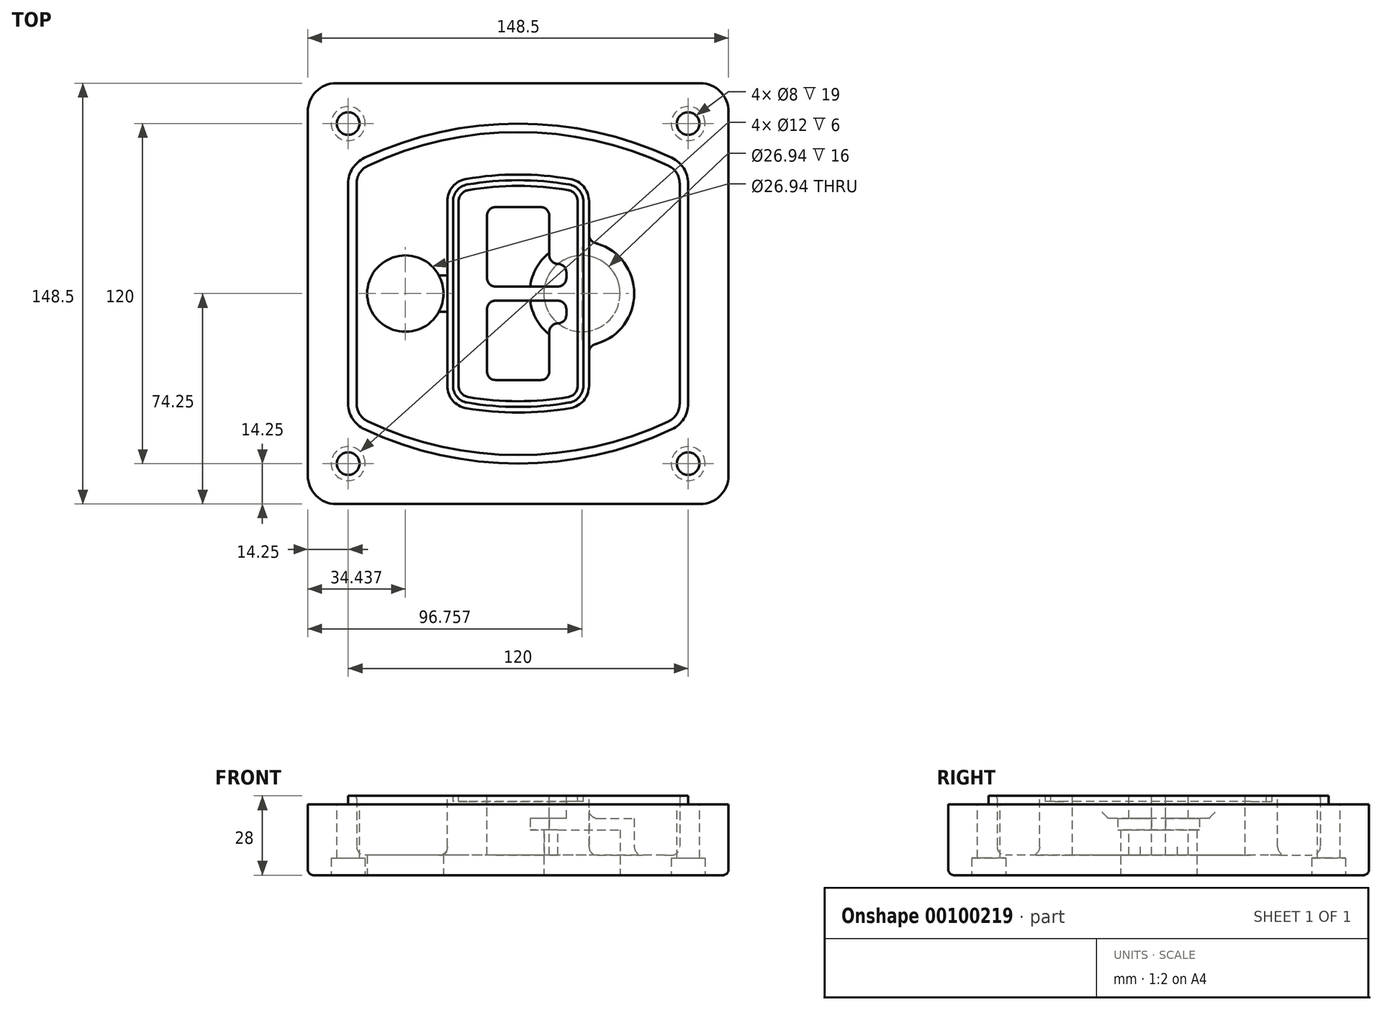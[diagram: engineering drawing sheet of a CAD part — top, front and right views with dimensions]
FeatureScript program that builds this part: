
annotation { "Feature Type Name" : "Feature", "Feature Type Description" : "" }
export const myFeature = defineFeature(function(context is Context, id is Id, definition is map)
    precondition{}
    {
        {
            var Q0;
            Q0=qCreatedBy(makeId("Top.planeOp"),FACE);
            var sketch = newSketch(context, id + "F0", { "sketchPlane" : qUnion([Q0])});
            skPoint(sketch, "E0.rect.middle", {"position": v(0, 0) * mm});
            skLineSegment(sketch, "E1.bottom", {"start": v(-64.25, -74.25) * mm, "end": v(64.25, -74.25) * mm});
            skLineSegment(sketch, "E1.top", {"start": v(-64.25, 74.25) * mm, "end": v(64.25, 74.25) * mm});
            skLineSegment(sketch, "E1.left", {"start": v(-74.25, -64.25) * mm, "end": v(-74.25, 64.25) * mm});
            skLineSegment(sketch, "E1.right", {"start": v(74.25, -64.25) * mm, "end": v(74.25, 64.25) * mm});
            skLineSegment(sketch, "E2", {"start": v(-74.25, 74.25) * mm, "end": v(74.25, -74.25) * mm, "construction": true});
            skLineSegment(sketch, "E3", {"start": v(74.25, 74.25) * mm, "end": v(-74.25, -74.25) * mm, "construction": true});
            skCircle(sketch, "E4", {"center": v(-60, 60) * mm, "radius": 4 * mm});
            skCircle(sketch, "E5", {"center": v(60, 60) * mm, "radius": 4 * mm});
            skCircle(sketch, "E6", {"center": v(60, -60) * mm, "radius": 4 * mm});
            skCircle(sketch, "E7", {"center": v(-60, -60) * mm, "radius": 4 * mm});
            skLineSegment(sketch, "E8", {"start": v(-60, 60) * mm, "end": v(60, 60) * mm, "construction": true});
            skLineSegment(sketch, "E9", {"start": v(60, 60) * mm, "end": v(60, -60) * mm, "construction": true});
            skLineSegment(sketch, "E10", {"start": v(60, -60) * mm, "end": v(-60, -60) * mm, "construction": true});
            skLineSegment(sketch, "E11", {"start": v(-60, -60) * mm, "end": v(-60, 60) * mm, "construction": true});
            skLineSegment(sketch, "E12", {"start": v(-60, 38.83) * mm, "end": v(-60, -38.83) * mm});
            skLineSegment(sketch, "E13", {"start": v(60, 38.83) * mm, "end": v(60, -38.83) * mm});
            skArc(sketch, "E14", {"start": v(54.26, 47.88) * mm, "mid": v(0, 60) * mm, "end": v(-54.26, 47.88) * mm});
            skArc(sketch, "E15", {"start": v(-54.26, -47.88) * mm, "mid": v(0, -60) * mm, "end": v(54.26, -47.88) * mm});
            skLineSegment(sketch, "E16", {"start": v(-60, 0) * mm, "end": v(60, 0) * mm, "construction": true});
            skPoint(sketch, "E17.visualSharp", {"position": v(-60, -45) * mm});
            skArc(sketch, "E17.filletArc", {"start": v(-60, -38.83) * mm, "mid": v(-58.44, -44.2) * mm, "end": v(-54.26, -47.88) * mm});
            skPoint(sketch, "E18.visualSharp", {"position": v(-60, 45) * mm});
            skArc(sketch, "E18.filletArc", {"start": v(-54.26, 47.88) * mm, "mid": v(-58.44, 44.2) * mm, "end": v(-60, 38.83) * mm});
            skPoint(sketch, "E19.visualSharp", {"position": v(60, 45) * mm});
            skArc(sketch, "E19.filletArc", {"start": v(60, 38.83) * mm, "mid": v(58.44, 44.2) * mm, "end": v(54.26, 47.88) * mm});
            skPoint(sketch, "E20.visualSharp", {"position": v(60, -45) * mm});
            skArc(sketch, "E20.filletArc", {"start": v(54.26, -47.88) * mm, "mid": v(58.44, -44.2) * mm, "end": v(60, -38.83) * mm});
            skPoint(sketch, "E21.visualSharp", {"position": v(-74.25, 74.25) * mm});
            skArc(sketch, "E21.filletArc", {"start": v(-64.25, 74.25) * mm, "mid": v(-71.32, 71.32) * mm, "end": v(-74.25, 64.25) * mm});
            skPoint(sketch, "E22.visualSharp", {"position": v(74.25, 74.25) * mm});
            skArc(sketch, "E22.filletArc", {"start": v(74.25, 64.25) * mm, "mid": v(71.32, 71.32) * mm, "end": v(64.25, 74.25) * mm});
            skPoint(sketch, "E23.visualSharp", {"position": v(74.25, -74.25) * mm});
            skArc(sketch, "E23.filletArc", {"start": v(64.25, -74.25) * mm, "mid": v(71.32, -71.32) * mm, "end": v(74.25, -64.25) * mm});
            skPoint(sketch, "E24.visualSharp", {"position": v(-74.25, -74.25) * mm});
            skArc(sketch, "E24.filletArc", {"start": v(-74.25, -64.25) * mm, "mid": v(-71.32, -71.32) * mm, "end": v(-64.25, -74.25) * mm});
            skArc(sketch, "E25.0", {"start": v(57, 38.83) * mm, "mid": v(55.9, 42.58) * mm, "end": v(52.98, 45.17) * mm});
            skLineSegment(sketch, "E25.1", {"start": v(57, 38.83) * mm, "end": v(57, -38.83) * mm});
            skArc(sketch, "E25.2", {"start": v(52.98, -45.17) * mm, "mid": v(55.9, -42.58) * mm, "end": v(57, -38.83) * mm});
            skArc(sketch, "E25.3", {"start": v(-52.98, -45.17) * mm, "mid": v(0, -57) * mm, "end": v(52.98, -45.17) * mm});
            skArc(sketch, "E25.4", {"start": v(-57, -38.83) * mm, "mid": v(-55.9, -42.58) * mm, "end": v(-52.98, -45.17) * mm});
            skArc(sketch, "E25.5", {"start": v(52.98, 45.17) * mm, "mid": v(0, 57) * mm, "end": v(-52.98, 45.17) * mm});
            skLineSegment(sketch, "E25.6", {"start": v(-57, 38.83) * mm, "end": v(-57, -38.83) * mm});
            skArc(sketch, "E25.7", {"start": v(-52.98, 45.17) * mm, "mid": v(-55.9, 42.58) * mm, "end": v(-57, 38.83) * mm});
            skArc(sketch, "E26.0", {"start": v(-55.96, 51.5) * mm, "mid": v(-61.82, 46.33) * mm, "end": v(-64, 38.83) * mm});
            skArc(sketch, "E26.1", {"start": v(55.96, 51.5) * mm, "mid": v(0, 64) * mm, "end": v(-55.96, 51.5) * mm});
            skArc(sketch, "E26.2", {"start": v(64, 38.83) * mm, "mid": v(61.82, 46.33) * mm, "end": v(55.96, 51.5) * mm});
            skLineSegment(sketch, "E26.3", {"start": v(64, 38.83) * mm, "end": v(64, -38.83) * mm});
            skArc(sketch, "E26.4", {"start": v(55.96, -51.5) * mm, "mid": v(61.82, -46.33) * mm, "end": v(64, -38.83) * mm});
            skLineSegment(sketch, "E26.5", {"start": v(-64, 38.83) * mm, "end": v(-64, -38.83) * mm});
            skArc(sketch, "E26.6", {"start": v(-55.96, -51.5) * mm, "mid": v(0, -64) * mm, "end": v(55.96, -51.5) * mm});
            skArc(sketch, "E26.7", {"start": v(-64, -38.83) * mm, "mid": v(-61.82, -46.33) * mm, "end": v(-55.96, -51.5) * mm});
            skSolve(sketch);
        }
        {
            var Q0;
            Q0=makeQuery(id+"F0.imprint","IMPRINT",FACE,{"disambiguationData":[TD([[makeQuery(id+"F0.imprint","IMPRINT",EDGE,{"derivedFrom":sQuery(id+"F0.wireOp",EDGE,"E1.bottom")}),1.0]])]});
            var Q1;
            Q1=makeQuery(id+"F0.imprint","IMPRINT",FACE,{"disambiguationData":[TD([[makeQuery(id+"F0.imprint","IMPRINT",EDGE,{"derivedFrom":sQuery(id+"F0.wireOp",EDGE,"E12")}),1.0]])]});
            var Q2;
            Q2=makeQuery(id+"F0.imprint","IMPRINT",FACE,{"disambiguationData":[TD([[makeQuery(id+"F0.imprint","IMPRINT",EDGE,{"derivedFrom":sQuery(id+"F0.wireOp",EDGE,"E25.0")}),1.0]])]});
            var Q3;
            Q3=makeQuery(id+"F0.imprint","IMPRINT",FACE,{"disambiguationData":[TD([[makeQuery(id+"F0.imprint","IMPRINT",EDGE,{"derivedFrom":sQuery(id+"F0.wireOp",EDGE,"E12")}),-1.0]])]});
            extrude(context, id + "F1", {"entities" : qUnion([Q0, Q1, Q2, Q3]), "oppositeDirection" : true, "depth" : 25 * mm});
        }
        {
            var Q0;
            Q0=makeQuery(id+"F0.imprint","IMPRINT",FACE,{"disambiguationData":[TD([[makeQuery(id+"F0.imprint","IMPRINT",EDGE,{"derivedFrom":sQuery(id+"F0.wireOp",EDGE,"E12")}),1.0]])]});
            extrude(context, id + "F2", {"entities" : qUnion([Q0]), "operationType" : NewBodyOperationType.ADD, "depth" : 3 * mm});
        }
        {
            var Q0;
            Q0=makeQuery(id+"F0.imprint","IMPRINT",FACE,{"disambiguationData":[TD([[makeQuery(id+"F0.imprint","IMPRINT",EDGE,{"derivedFrom":sQuery(id+"F0.wireOp",EDGE,"E25.0")}),1.0]])]});
            extrude(context, id + "F3", {"entities" : qUnion([Q0]), "operationType" : NewBodyOperationType.REMOVE, "oppositeDirection" : true, "depth" : 18 * mm});
        }
        {
            var Q0;
            Q0=makeQuery(id+"F2.opExtrude","CAP_FACE",FACE,{"disambiguationData":[OSD([sQuery(id+"F0.wireOp",EDGE,"E12"),sQuery(id+"F0.wireOp",EDGE,"E13"),sQuery(id+"F0.wireOp",EDGE,"E14"),sQuery(id+"F0.wireOp",EDGE,"E15"),sQuery(id+"F0.wireOp",EDGE,"E17.filletArc"),sQuery(id+"F0.wireOp",EDGE,"E18.filletArc"),sQuery(id+"F0.wireOp",EDGE,"E19.filletArc"),sQuery(id+"F0.wireOp",EDGE,"E20.filletArc"),sQuery(id+"F0.wireOp",EDGE,"E25.0"),sQuery(id+"F0.wireOp",EDGE,"E25.1"),sQuery(id+"F0.wireOp",EDGE,"E25.2"),sQuery(id+"F0.wireOp",EDGE,"E25.3"),sQuery(id+"F0.wireOp",EDGE,"E25.4"),sQuery(id+"F0.wireOp",EDGE,"E25.5"),sQuery(id+"F0.wireOp",EDGE,"E25.6"),sQuery(id+"F0.wireOp",EDGE,"E25.7")])],"isStart":false});
            var sketch = newSketch(context, id + "F4", { "sketchPlane" : qUnion([Q0])});
            skArc(sketch, "E27.0", {"start": v(-18.34, -40.45) * mm, "mid": v(0, -42) * mm, "end": v(18.34, -40.45) * mm});
            skArc(sketch, "E28.0", {"start": v(18.34, 40.45) * mm, "mid": v(0, 42) * mm, "end": v(-18.34, 40.45) * mm});
            skLineSegment(sketch, "E29", {"start": v(-25, 32.57) * mm, "end": v(-25, -32.57) * mm});
            skLineSegment(sketch, "E30", {"start": v(25, 32.57) * mm, "end": v(25, -32.57) * mm});
            skLineSegment(sketch, "E31", {"start": v(-25, 39.1) * mm, "end": v(25, 39.1) * mm, "construction": true});
            skLineSegment(sketch, "E32", {"start": v(-25, -39.1) * mm, "end": v(25, -39.1) * mm, "construction": true});
            skPoint(sketch, "E33.visualSharp", {"position": v(-25, 39.1) * mm});
            skArc(sketch, "E33.filletArc", {"start": v(-18.34, 40.45) * mm, "mid": v(-23.11, 37.73) * mm, "end": v(-25, 32.57) * mm});
            skPoint(sketch, "E34.visualSharp", {"position": v(25, 39.1) * mm});
            skArc(sketch, "E34.filletArc", {"start": v(25, 32.57) * mm, "mid": v(23.11, 37.73) * mm, "end": v(18.34, 40.45) * mm});
            skPoint(sketch, "E35.visualSharp", {"position": v(25, -39.1) * mm});
            skArc(sketch, "E35.filletArc", {"start": v(18.34, -40.45) * mm, "mid": v(23.11, -37.73) * mm, "end": v(25, -32.57) * mm});
            skPoint(sketch, "E36.visualSharp", {"position": v(-25, -39.1) * mm});
            skArc(sketch, "E36.filletArc", {"start": v(-25, -32.57) * mm, "mid": v(-23.11, -37.73) * mm, "end": v(-18.34, -40.45) * mm});
            skArc(sketch, "E37.0", {"start": v(52.98, 45.17) * mm, "mid": v(0, 57) * mm, "end": v(-52.98, 45.17) * mm});
            skArc(sketch, "E37.1", {"start": v(-52.98, 45.17) * mm, "mid": v(-55.9, 42.58) * mm, "end": v(-57, 38.83) * mm});
            skLineSegment(sketch, "E37.2", {"start": v(-57, 38.83) * mm, "end": v(-57, -38.83) * mm});
            skArc(sketch, "E37.3", {"start": v(-57, -38.83) * mm, "mid": v(-55.9, -42.58) * mm, "end": v(-52.98, -45.17) * mm});
            skArc(sketch, "E37.4", {"start": v(-52.98, -45.17) * mm, "mid": v(0, -57) * mm, "end": v(52.98, -45.17) * mm});
            skArc(sketch, "E37.5", {"start": v(52.98, -45.17) * mm, "mid": v(55.9, -42.58) * mm, "end": v(57, -38.83) * mm});
            skLineSegment(sketch, "E37.6", {"start": v(57, 38.83) * mm, "end": v(57, -38.83) * mm});
            skArc(sketch, "E37.7", {"start": v(57, 38.83) * mm, "mid": v(55.9, 42.58) * mm, "end": v(52.98, 45.17) * mm});
            skLineSegment(sketch, "E38.0", {"start": v(23, 32.57) * mm, "end": v(23, -32.57) * mm});
            skArc(sketch, "E38.1", {"start": v(18, -38.48) * mm, "mid": v(21.58, -36.44) * mm, "end": v(23, -32.57) * mm});
            skArc(sketch, "E38.2", {"start": v(-18, -38.48) * mm, "mid": v(0, -40) * mm, "end": v(18, -38.48) * mm});
            skArc(sketch, "E38.3", {"start": v(-23, -32.57) * mm, "mid": v(-21.58, -36.44) * mm, "end": v(-18, -38.48) * mm});
            skLineSegment(sketch, "E38.4", {"start": v(-23, 32.57) * mm, "end": v(-23, -32.57) * mm});
            skArc(sketch, "E38.5", {"start": v(23, 32.57) * mm, "mid": v(21.58, 36.44) * mm, "end": v(18, 38.48) * mm});
            skArc(sketch, "E38.6", {"start": v(-18, 38.48) * mm, "mid": v(-21.58, 36.44) * mm, "end": v(-23, 32.57) * mm});
            skArc(sketch, "E38.7", {"start": v(18, 38.48) * mm, "mid": v(0, 40) * mm, "end": v(-18, 38.48) * mm});
            skArc(sketch, "E39.0", {"start": v(21, 32.57) * mm, "mid": v(20.06, 35.15) * mm, "end": v(17.67, 36.5) * mm});
            skLineSegment(sketch, "E39.1", {"start": v(21, 32.57) * mm, "end": v(21, -32.57) * mm});
            skArc(sketch, "E39.2", {"start": v(17.67, -36.5) * mm, "mid": v(20.06, -35.15) * mm, "end": v(21, -32.57) * mm});
            skArc(sketch, "E39.3", {"start": v(-17.67, -36.5) * mm, "mid": v(0, -38) * mm, "end": v(17.67, -36.5) * mm});
            skArc(sketch, "E39.4", {"start": v(-21, -32.57) * mm, "mid": v(-20.06, -35.15) * mm, "end": v(-17.67, -36.5) * mm});
            skArc(sketch, "E39.5", {"start": v(17.67, 36.5) * mm, "mid": v(0, 38) * mm, "end": v(-17.67, 36.5) * mm});
            skLineSegment(sketch, "E39.6", {"start": v(-21, 32.57) * mm, "end": v(-21, -32.57) * mm});
            skArc(sketch, "E39.7", {"start": v(-17.67, 36.5) * mm, "mid": v(-20.06, 35.15) * mm, "end": v(-21, 32.57) * mm});
            skLineSegment(sketch, "E40", {"start": v(-25, 0) * mm, "end": v(25, 0) * mm, "construction": true});
            skLineSegment(sketch, "E41", {"start": v(-11, 5.5) * mm, "end": v(-11, 27.5) * mm});
            skLineSegment(sketch, "E42", {"start": v(-8, 30.5) * mm, "end": v(8, 30.5) * mm});
            skLineSegment(sketch, "E43", {"start": v(11, 27.5) * mm, "end": v(11, 13.5) * mm});
            skLineSegment(sketch, "E44", {"start": v(14, 10.5) * mm, "end": v(14, 10.5) * mm});
            skLineSegment(sketch, "E45", {"start": v(17, 7.5) * mm, "end": v(17, 5.5) * mm});
            skLineSegment(sketch, "E46", {"start": v(14, 2.5) * mm, "end": v(-8, 2.5) * mm});
            skPoint(sketch, "E47.visualSharp", {"position": v(-11, 30.5) * mm});
            skArc(sketch, "E47.filletArc", {"start": v(-8, 30.5) * mm, "mid": v(-10.12, 29.62) * mm, "end": v(-11, 27.5) * mm});
            skPoint(sketch, "E48.visualSharp", {"position": v(11, 30.5) * mm});
            skArc(sketch, "E48.filletArc", {"start": v(11, 27.5) * mm, "mid": v(10.12, 29.62) * mm, "end": v(8, 30.5) * mm});
            skPoint(sketch, "E49.visualSharp", {"position": v(11, 10.5) * mm});
            skArc(sketch, "E49.filletArc", {"start": v(11, 13.5) * mm, "mid": v(11.88, 11.38) * mm, "end": v(14, 10.5) * mm});
            skPoint(sketch, "E50.visualSharp", {"position": v(17, 10.5) * mm});
            skArc(sketch, "E50.filletArc", {"start": v(17, 7.5) * mm, "mid": v(16.12, 9.62) * mm, "end": v(14, 10.5) * mm});
            skPoint(sketch, "E51.visualSharp", {"position": v(17, 2.5) * mm});
            skArc(sketch, "E51.filletArc", {"start": v(14, 2.5) * mm, "mid": v(16.12, 3.38) * mm, "end": v(17, 5.5) * mm});
            skPoint(sketch, "E52.visualSharp", {"position": v(-11, 2.5) * mm});
            skArc(sketch, "E52.filletArc", {"start": v(-11, 5.5) * mm, "mid": v(-10.12, 3.38) * mm, "end": v(-8, 2.5) * mm});
            skLineSegment(sketch, "E53.0.MirrorCS", {"start": v(14, -2.5) * mm, "end": v(-8, -2.5) * mm});
            skArc(sketch, "E54.0.MirrorCS", {"start": v(-11, -5.5) * mm, "mid": v(-10.12, -3.38) * mm, "end": v(-8, -2.5) * mm});
            skLineSegment(sketch, "E55.0.MirrorCS", {"start": v(-11, -5.5) * mm, "end": v(-11, -27.5) * mm});
            skArc(sketch, "E56.0.MirrorCS", {"start": v(-8, -30.5) * mm, "mid": v(-10.12, -29.62) * mm, "end": v(-11, -27.5) * mm});
            skLineSegment(sketch, "E57.0.MirrorCS", {"start": v(-8, -30.5) * mm, "end": v(8, -30.5) * mm});
            skArc(sketch, "E58.0.MirrorCS", {"start": v(11, -27.5) * mm, "mid": v(10.12, -29.62) * mm, "end": v(8, -30.5) * mm});
            skLineSegment(sketch, "E59.0.MirrorCS", {"start": v(11, -27.5) * mm, "end": v(11, -13.5) * mm});
            skArc(sketch, "E60.0.MirrorCS", {"start": v(11, -13.5) * mm, "mid": v(11.88, -11.38) * mm, "end": v(14, -10.5) * mm});
            skArc(sketch, "E61.0.MirrorCS", {"start": v(17, -7.5) * mm, "mid": v(16.12, -9.62) * mm, "end": v(14, -10.5) * mm});
            skLineSegment(sketch, "E62.0.MirrorCS", {"start": v(17, -7.5) * mm, "end": v(17, -5.5) * mm});
            skArc(sketch, "E63.0.MirrorCS", {"start": v(14, -2.5) * mm, "mid": v(16.12, -3.38) * mm, "end": v(17, -5.5) * mm});
            skSolve(sketch);
        }
        {
            var Q0;
            Q0=makeQuery(id+"F4.imprint","IMPRINT",FACE,{"disambiguationData":[TD([[makeQuery(id+"F4.imprint","IMPRINT",EDGE,{"derivedFrom":sQuery(id+"F4.wireOp",EDGE,"E27.0")}),1.0]])]});
            var Q1;
            Q1=makeQuery(id+"F4.imprint","IMPRINT",FACE,{"disambiguationData":[TD([[makeQuery(id+"F4.imprint","IMPRINT",EDGE,{"derivedFrom":sQuery(id+"F4.wireOp",EDGE,"E38.0")}),-1.0]])]});
            var Q2;
            Q2=makeQuery(id+"F4.imprint","IMPRINT",FACE,{"disambiguationData":[TD([[makeQuery(id+"F4.imprint","IMPRINT",EDGE,{"derivedFrom":sQuery(id+"F4.wireOp",EDGE,"E39.0")}),1.0]])]});
            extrude(context, id + "F5", {"entities" : qUnion([Q0, Q1, Q2]), "operationType" : NewBodyOperationType.ADD, "endBound" : BoundingType.UP_TO_NEXT, "oppositeDirection" : true, "depth" : 25 * mm});
        }
        {
            var Q0;
            Q0=makeQuery(id+"F4.imprint","IMPRINT",FACE,{"disambiguationData":[TD([[makeQuery(id+"F4.imprint","IMPRINT",EDGE,{"derivedFrom":sQuery(id+"F4.wireOp",EDGE,"E38.0")}),-1.0]])]});
            extrude(context, id + "F6", {"entities" : qUnion([Q0]), "operationType" : NewBodyOperationType.REMOVE, "oppositeDirection" : true, "depth" : 2 * mm});
        }
        {
            var Q0;
            Q0=makeQuery(id+"F1.opExtrude","CAP_FACE",FACE,{"disambiguationData":[OSD([sQuery(id+"F0.wireOp",EDGE,"E1.bottom"),sQuery(id+"F0.wireOp",EDGE,"E1.top"),sQuery(id+"F0.wireOp",EDGE,"E1.left"),sQuery(id+"F0.wireOp",EDGE,"E1.right"),sQuery(id+"F0.wireOp",EDGE,"E4"),sQuery(id+"F0.wireOp",EDGE,"E5"),sQuery(id+"F0.wireOp",EDGE,"E6"),sQuery(id+"F0.wireOp",EDGE,"E7"),sQuery(id+"F0.wireOp",EDGE,"E21.filletArc"),sQuery(id+"F0.wireOp",EDGE,"E22.filletArc"),sQuery(id+"F0.wireOp",EDGE,"E23.filletArc"),sQuery(id+"F0.wireOp",EDGE,"E24.filletArc")])],"isStart":false});
            var sketch = newSketch(context, id + "F7", { "sketchPlane" : qUnion([Q0])});
            skCircle(sketch, "E64", {"center": v(22.5, 0) * mm, "radius": 13.47 * mm});
            skCircle(sketch, "E65", {"center": v(-39.81, 0) * mm, "radius": 13.47 * mm});
            skLineSegment(sketch, "E66", {"start": v(74.25, 0) * mm, "end": v(-74.25, 0) * mm});
            skCircle(sketch, "E67", {"center": v(22.5, 0) * mm, "radius": 18.47 * mm});
            skCircle(sketch, "E68", {"center": v(60, -60) * mm, "radius": 6 * mm});
            skCircle(sketch, "E69", {"center": v(-60, -60) * mm, "radius": 6 * mm});
            skCircle(sketch, "E70", {"center": v(-60, 60) * mm, "radius": 6 * mm});
            skCircle(sketch, "E71", {"center": v(60, 60) * mm, "radius": 6 * mm});
            skSolve(sketch);
        }
        {
            var Q0;
            {var subQ1=sQuery(id+"F7.wireOp",EDGE,"E66");var subQ4=sQuery(id+"F7.wireOp",EDGE,"E64");var subQ6=makeQuery(id+"F7.imprint","INTERSECT",VERTEX,{"disambiguationData":[OD(0.0)],"derivedFrom":[subQ4,subQ1]});Q0=makeQuery(id+"F7.imprint","IMPRINT",FACE,{"disambiguationData":[TD([[makeQuery(id+"F7.imprint","IMPRINT",EDGE,{"disambiguationData":[TD([[subQ6,-1.0]])],"derivedFrom":subQ4}),-1.0]])]});}
            var Q1;
            {var subQ0=sQuery(id+"F7.wireOp",EDGE,"E66");var subQ1=sQuery(id+"F7.wireOp",EDGE,"E64");var subQ3=makeQuery(id+"F7.imprint","INTERSECT",VERTEX,{"disambiguationData":[OD(0.0)],"derivedFrom":[subQ1,subQ0]});Q1=makeQuery(id+"F7.imprint","IMPRINT",FACE,{"disambiguationData":[TD([[makeQuery(id+"F7.imprint","IMPRINT",EDGE,{"disambiguationData":[TD([[subQ3,-1.0]])],"derivedFrom":subQ1}),1.0]])]});}
            var Q2;
            {var subQ0=sQuery(id+"F7.wireOp",EDGE,"E66");var subQ1=sQuery(id+"F7.wireOp",EDGE,"E64");var subQ3=makeQuery(id+"F7.imprint","INTERSECT",VERTEX,{"disambiguationData":[OD(0.0)],"derivedFrom":[subQ1,subQ0]});Q2=makeQuery(id+"F7.imprint","IMPRINT",FACE,{"disambiguationData":[TD([[makeQuery(id+"F7.imprint","IMPRINT",EDGE,{"disambiguationData":[TD([[subQ3,1.0]])],"derivedFrom":subQ1}),1.0]])]});}
            var Q3;
            {var subQ1=sQuery(id+"F7.wireOp",EDGE,"E66");var subQ4=sQuery(id+"F7.wireOp",EDGE,"E64");var subQ6=makeQuery(id+"F7.imprint","INTERSECT",VERTEX,{"disambiguationData":[OD(0.0)],"derivedFrom":[subQ4,subQ1]});Q3=makeQuery(id+"F7.imprint","IMPRINT",FACE,{"disambiguationData":[TD([[makeQuery(id+"F7.imprint","IMPRINT",EDGE,{"disambiguationData":[TD([[subQ6,1.0]])],"derivedFrom":subQ4}),-1.0]])]});}
            extrude(context, id + "F8", {"entities" : qUnion([Q0, Q1, Q2, Q3]), "operationType" : NewBodyOperationType.ADD, "oppositeDirection" : true, "depth" : 20 * mm});
        }
        {
            var Q0;
            {var subQ0=sQuery(id+"F7.wireOp",EDGE,"E66");var subQ1=sQuery(id+"F7.wireOp",EDGE,"E64");var subQ3=makeQuery(id+"F7.imprint","INTERSECT",VERTEX,{"disambiguationData":[OD(0.0)],"derivedFrom":[subQ1,subQ0]});Q0=makeQuery(id+"F7.imprint","IMPRINT",FACE,{"disambiguationData":[TD([[makeQuery(id+"F7.imprint","IMPRINT",EDGE,{"disambiguationData":[TD([[subQ3,-1.0]])],"derivedFrom":subQ1}),1.0]])]});}
            var Q1;
            {var subQ0=sQuery(id+"F7.wireOp",EDGE,"E66");var subQ1=sQuery(id+"F7.wireOp",EDGE,"E64");var subQ3=makeQuery(id+"F7.imprint","INTERSECT",VERTEX,{"disambiguationData":[OD(0.0)],"derivedFrom":[subQ1,subQ0]});Q1=makeQuery(id+"F7.imprint","IMPRINT",FACE,{"disambiguationData":[TD([[makeQuery(id+"F7.imprint","IMPRINT",EDGE,{"disambiguationData":[TD([[subQ3,1.0]])],"derivedFrom":subQ1}),1.0]])]});}
            extrude(context, id + "F9", {"entities" : qUnion([Q0, Q1]), "operationType" : NewBodyOperationType.REMOVE, "oppositeDirection" : true, "depth" : 16 * mm});
        }
        {
            var Q0;
            {var subQ0=sQuery(id+"F7.wireOp",EDGE,"E66");var subQ1=sQuery(id+"F7.wireOp",EDGE,"E65");var subQ3=makeQuery(id+"F7.imprint","INTERSECT",VERTEX,{"disambiguationData":[OD(0.0)],"derivedFrom":[subQ1,subQ0]});Q0=makeQuery(id+"F7.imprint","IMPRINT",FACE,{"disambiguationData":[TD([[makeQuery(id+"F7.imprint","IMPRINT",EDGE,{"disambiguationData":[TD([[subQ3,-1.0]])],"derivedFrom":subQ1}),1.0]])]});}
            var Q1;
            {var subQ0=sQuery(id+"F7.wireOp",EDGE,"E66");var subQ1=sQuery(id+"F7.wireOp",EDGE,"E65");var subQ3=makeQuery(id+"F7.imprint","INTERSECT",VERTEX,{"disambiguationData":[OD(0.0)],"derivedFrom":[subQ1,subQ0]});Q1=makeQuery(id+"F7.imprint","IMPRINT",FACE,{"disambiguationData":[TD([[makeQuery(id+"F7.imprint","IMPRINT",EDGE,{"disambiguationData":[TD([[subQ3,1.0]])],"derivedFrom":subQ1}),1.0]])]});}
            extrude(context, id + "F10", {"entities" : qUnion([Q0, Q1]), "operationType" : NewBodyOperationType.REMOVE, "oppositeDirection" : true, "depth" : 25 * mm});
        }
        {
            var Q0;
            Q0=makeQuery(id+"F7.imprint","IMPRINT",FACE,{"disambiguationData":[TD([[makeQuery(id+"F7.imprint","IMPRINT",EDGE,{"derivedFrom":sQuery(id+"F7.wireOp",EDGE,"E68")}),1.0]])]});
            var Q1;
            Q1=makeQuery(id+"F7.imprint","IMPRINT",FACE,{"disambiguationData":[TD([[makeQuery(id+"F7.imprint","IMPRINT",EDGE,{"derivedFrom":makeQuery(id+"F1.opExtrude","CAP_EDGE",EDGE,{"disambiguationData":[OSD([sQuery(id+"F0.wireOp",EDGE,"E5")])],"isStart":false})}),-1.0]])]});
            var Q2;
            Q2=makeQuery(id+"F7.imprint","IMPRINT",FACE,{"disambiguationData":[TD([[makeQuery(id+"F7.imprint","IMPRINT",EDGE,{"derivedFrom":sQuery(id+"F7.wireOp",EDGE,"E69")}),1.0]])]});
            var Q3;
            Q3=makeQuery(id+"F7.imprint","IMPRINT",FACE,{"disambiguationData":[TD([[makeQuery(id+"F7.imprint","IMPRINT",EDGE,{"derivedFrom":makeQuery(id+"F1.opExtrude","CAP_EDGE",EDGE,{"disambiguationData":[OSD([sQuery(id+"F0.wireOp",EDGE,"E4")])],"isStart":false})}),-1.0]])]});
            var Q4;
            Q4=makeQuery(id+"F7.imprint","IMPRINT",FACE,{"disambiguationData":[TD([[makeQuery(id+"F7.imprint","IMPRINT",EDGE,{"derivedFrom":sQuery(id+"F7.wireOp",EDGE,"E70")}),1.0]])]});
            var Q5;
            Q5=makeQuery(id+"F7.imprint","IMPRINT",FACE,{"disambiguationData":[TD([[makeQuery(id+"F7.imprint","IMPRINT",EDGE,{"derivedFrom":makeQuery(id+"F1.opExtrude","CAP_EDGE",EDGE,{"disambiguationData":[OSD([sQuery(id+"F0.wireOp",EDGE,"E7")])],"isStart":false})}),-1.0]])]});
            var Q6;
            Q6=makeQuery(id+"F7.imprint","IMPRINT",FACE,{"disambiguationData":[TD([[makeQuery(id+"F7.imprint","IMPRINT",EDGE,{"derivedFrom":sQuery(id+"F7.wireOp",EDGE,"E71")}),1.0]])]});
            var Q7;
            Q7=makeQuery(id+"F7.imprint","IMPRINT",FACE,{"disambiguationData":[TD([[makeQuery(id+"F7.imprint","IMPRINT",EDGE,{"derivedFrom":makeQuery(id+"F1.opExtrude","CAP_EDGE",EDGE,{"disambiguationData":[OSD([sQuery(id+"F0.wireOp",EDGE,"E6")])],"isStart":false})}),-1.0]])]});
            extrude(context, id + "F11", {"entities" : qUnion([Q0, Q1, Q2, Q3, Q4, Q5, Q6, Q7]), "operationType" : NewBodyOperationType.REMOVE, "oppositeDirection" : true, "depth" : 6 * mm});
        }
        {
            var Q0;
            Q0=makeQuery(id+"F9.boolean.opBoolean","COPY",FACE,{"derivedFrom":makeQuery(id+"F9.opExtrude","CAP_FACE",FACE,{"disambiguationData":[OSD([sQuery(id+"F7.wireOp",EDGE,"E64")])],"isStart":false})});
            var sketch = newSketch(context, id + "F12", { "sketchPlane" : qUnion([Q0])});
            skArc(sketch, "E72.0", {"start": v(11, 14.45) * mm, "mid": v(6.45, 9.13) * mm, "end": v(4.2, 2.5) * mm});
            skArc(sketch, "E72.1", {"start": v(4.2, -2.5) * mm, "mid": v(6.45, -9.13) * mm, "end": v(11, -14.45) * mm});
            skLineSegment(sketch, "E73", {"start": v(4.2, -2.5) * mm, "end": v(14, -2.5) * mm});
            skLineSegment(sketch, "E74.0", {"start": v(14, 2.5) * mm, "end": v(4.2, 2.5) * mm});
            skArc(sketch, "E74.1", {"start": v(14, 2.5) * mm, "mid": v(16.12, 3.38) * mm, "end": v(17, 5.5) * mm});
            skLineSegment(sketch, "E74.2", {"start": v(17, 7.5) * mm, "end": v(17, 5.5) * mm});
            skArc(sketch, "E74.3", {"start": v(17, 7.5) * mm, "mid": v(16.12, 9.62) * mm, "end": v(14, 10.5) * mm});
            skArc(sketch, "E74.4", {"start": v(11, 13.5) * mm, "mid": v(11.88, 11.38) * mm, "end": v(14, 10.5) * mm});
            skLineSegment(sketch, "E74.5", {"start": v(11, 14.45) * mm, "end": v(11, 13.5) * mm});
            skLineSegment(sketch, "E74.7", {"start": v(14, -2.5) * mm, "end": v(4.2, -2.5) * mm});
            skArc(sketch, "E74.8", {"start": v(14, -2.5) * mm, "mid": v(16.12, -3.38) * mm, "end": v(17, -5.5) * mm});
            skLineSegment(sketch, "E74.9", {"start": v(17, -7.5) * mm, "end": v(17, -5.5) * mm});
            skArc(sketch, "E74.10", {"start": v(17, -7.5) * mm, "mid": v(16.12, -9.62) * mm, "end": v(14, -10.5) * mm});
            skArc(sketch, "E74.11", {"start": v(11, -13.5) * mm, "mid": v(11.88, -11.38) * mm, "end": v(14, -10.5) * mm});
            skLineSegment(sketch, "E74.12", {"start": v(11, -14.45) * mm, "end": v(11, -13.5) * mm});
            skPoint(sketch, "E75.orphan", {"position": v(11, -27.5) * mm});
            skPoint(sketch, "E76.orphan", {"position": v(-8, -2.5) * mm});
            skPoint(sketch, "E77.orphan", {"position": v(-8, 2.5) * mm});
            skPoint(sketch, "E78.orphan", {"position": v(11, 27.5) * mm});
            skSolve(sketch);
        }
        {
            var Q0;
            {var subQ7=sQuery(id+"F12.wireOp",EDGE,"E72.0");var subQ14=sQuery(id+"F12.wireOp",EDGE,"E72.1");var subQ16=sQuery(id+"F12.wireOp",EDGE,"E74.1");var subQ18=sQuery(id+"F12.wireOp",EDGE,"E74.8");Q0=qUnion([makeQuery(id+"F12.imprint","IMPRINT",FACE,{"disambiguationData":[TD([[makeQuery(id+"F12.imprint","IMPRINT",EDGE,{"derivedFrom":subQ7}),1.0]])]}),makeQuery(id+"F12.imprint","IMPRINT",FACE,{"disambiguationData":[TD([[makeQuery(id+"F12.imprint","IMPRINT",EDGE,{"derivedFrom":subQ14}),1.0]])]}),makeQuery(id+"F12.imprint","IMPRINT",FACE,{"disambiguationData":[TD([[makeQuery(id+"F12.imprint","IMPRINT",EDGE,{"derivedFrom":subQ16}),1.0]])]}),makeQuery(id+"F12.imprint","IMPRINT",FACE,{"disambiguationData":[TD([[makeQuery(id+"F12.imprint","IMPRINT",EDGE,{"derivedFrom":subQ18}),-1.0]])]})]);}
            var Q1;
            Q1=makeQuery(id+"F5.boolean.opBoolean","SPLIT",FACE,{"disambiguationData":[TD([makeQuery(id+"F5.opExtrude","SWEPT_FACE",FACE,{"disambiguationData":[OSD([sQuery(id+"F4.wireOp",EDGE,"E41")])]})])],"derivedFrom":makeQuery(id+"F3.boolean.opBoolean","COPY",FACE,{"derivedFrom":makeQuery(id+"F3.opExtrude","CAP_FACE",FACE,{"disambiguationData":[OSD([sQuery(id+"F0.wireOp",EDGE,"E25.0"),sQuery(id+"F0.wireOp",EDGE,"E25.1"),sQuery(id+"F0.wireOp",EDGE,"E25.2"),sQuery(id+"F0.wireOp",EDGE,"E25.3"),sQuery(id+"F0.wireOp",EDGE,"E25.4"),sQuery(id+"F0.wireOp",EDGE,"E25.5"),sQuery(id+"F0.wireOp",EDGE,"E25.6"),sQuery(id+"F0.wireOp",EDGE,"E25.7")])],"isStart":false})})});
            extrude(context, id + "F13", {"entities" : qUnion([Q0]), "operationType" : NewBodyOperationType.REMOVE, "endBound" : BoundingType.UP_TO_SURFACE, "endBoundEntityFace" : qUnion([Q1]), "depth" : 25 * mm});
        }
        {
            var Q0;
            Q0=makeQuery(id+"F3.boolean.opBoolean","COPY",EDGE,{"derivedFrom":makeQuery(id+"F3.opExtrude","CAP_EDGE",EDGE,{"disambiguationData":[OSD([sQuery(id+"F0.wireOp",EDGE,"E25.6")])],"isStart":false})});
            var Q1;
            Q1=makeQuery(id+"F8.boolean.opBoolean","INTERSECT",EDGE,{"derivedFrom":[makeQuery(id+"F5.opExtrude","SWEPT_FACE",FACE,{"disambiguationData":[OSD([sQuery(id+"F4.wireOp",EDGE,"E30")])]}),makeQuery(id+"F8.opExtrude","CAP_FACE",FACE,{"disambiguationData":[OSD([sQuery(id+"F7.wireOp",EDGE,"E67")])],"isStart":false})]});
            var Q2;
            Q2=makeQuery(id+"F8.boolean.opBoolean","INTERSECT",EDGE,{"disambiguationData":[OD(1.0)],"derivedFrom":[makeQuery(id+"F5.opExtrude","SWEPT_FACE",FACE,{"disambiguationData":[OSD([sQuery(id+"F4.wireOp",EDGE,"E30")])]}),makeQuery(id+"F8.opExtrude","SWEPT_FACE",FACE,{"disambiguationData":[OSD([sQuery(id+"F7.wireOp",EDGE,"E67")])]})]});
            var Q3;
            {var subQ0=sQuery(id+"F4.wireOp",EDGE,"E30");Q3=makeQuery(id+"F8.boolean.opBoolean","SPLIT",EDGE,{"disambiguationData":[TD([makeQuery(id+"F5.opExtrude","SWEPT_FACE",FACE,{"disambiguationData":[OSD([sQuery(id+"F4.wireOp",EDGE,"E35.filletArc")])]})])],"derivedFrom":makeQuery(id+"F5.opExtrude","CAP_EDGE",EDGE,{"disambiguationData":[OSD([subQ0])],"isStart":false})});}
            var Q4;
            {var subQ0=sQuery(id+"F0.wireOp",EDGE,"E25.7");var subQ1=sQuery(id+"F0.wireOp",EDGE,"E25.1");var subQ2=sQuery(id+"F0.wireOp",EDGE,"E25.6");var subQ3=sQuery(id+"F0.wireOp",EDGE,"E25.5");var subQ4=sQuery(id+"F0.wireOp",EDGE,"E25.4");var subQ5=sQuery(id+"F0.wireOp",EDGE,"E25.0");var subQ6=sQuery(id+"F0.wireOp",EDGE,"E25.2");var subQ7=sQuery(id+"F0.wireOp",EDGE,"E25.3");Q4=makeQuery(id+"F8.boolean.opBoolean","INTERSECT",EDGE,{"derivedFrom":[makeQuery(id+"F5.boolean.opBoolean","SPLIT",FACE,{"disambiguationData":[TD([makeQuery(id+"F2.opExtrude","SWEPT_FACE",FACE,{"disambiguationData":[OSD([subQ5])]})])],"derivedFrom":makeQuery(id+"F3.boolean.opBoolean","COPY",FACE,{"derivedFrom":makeQuery(id+"F3.opExtrude","CAP_FACE",FACE,{"disambiguationData":[OSD([subQ5,subQ1,subQ6,subQ7,subQ4,subQ3,subQ2,subQ0])],"isStart":false})})}),makeQuery(id+"F8.opExtrude","SWEPT_FACE",FACE,{"disambiguationData":[OSD([sQuery(id+"F7.wireOp",EDGE,"E67")])]})]});}
            var Q5;
            Q5=makeQuery(id+"F8.boolean.opBoolean","INTERSECT",EDGE,{"disambiguationData":[OD(0.0)],"derivedFrom":[makeQuery(id+"F5.opExtrude","SWEPT_FACE",FACE,{"disambiguationData":[OSD([sQuery(id+"F4.wireOp",EDGE,"E30")])]}),makeQuery(id+"F8.opExtrude","SWEPT_FACE",FACE,{"disambiguationData":[OSD([sQuery(id+"F7.wireOp",EDGE,"E67")])]})]});
            fillet(context, id + "F14", {"entities" : qUnion([Q0, Q1, Q2, Q3, Q4, Q5]), "radius" : 3 * mm, "tangentPropagation" : true, "allowEdgeOverflow" : false});
        }
        {
            var Q0;
            Q0=makeQuery(id+"F1.opExtrude","CAP_EDGE",EDGE,{"disambiguationData":[OSD([sQuery(id+"F0.wireOp",EDGE,"E1.bottom")])],"isStart":false});
            fillet(context, id + "F15", {"entities" : qUnion([Q0]), "radius" : 2 * mm, "tangentPropagation" : true, "allowEdgeOverflow" : false});
        }
        {
            var Q0;
            Q0=makeQuery(id+"F2.opExtrude","CAP_EDGE",EDGE,{"disambiguationData":[OSD([sQuery(id+"F0.wireOp",EDGE,"E25.6")])],"isStart":false});
            fillet(context, id + "F16", {"entities" : qUnion([Q0]), "radius" : 1 * mm, "tangentPropagation" : true, "allowEdgeOverflow" : false});
        }
    });
